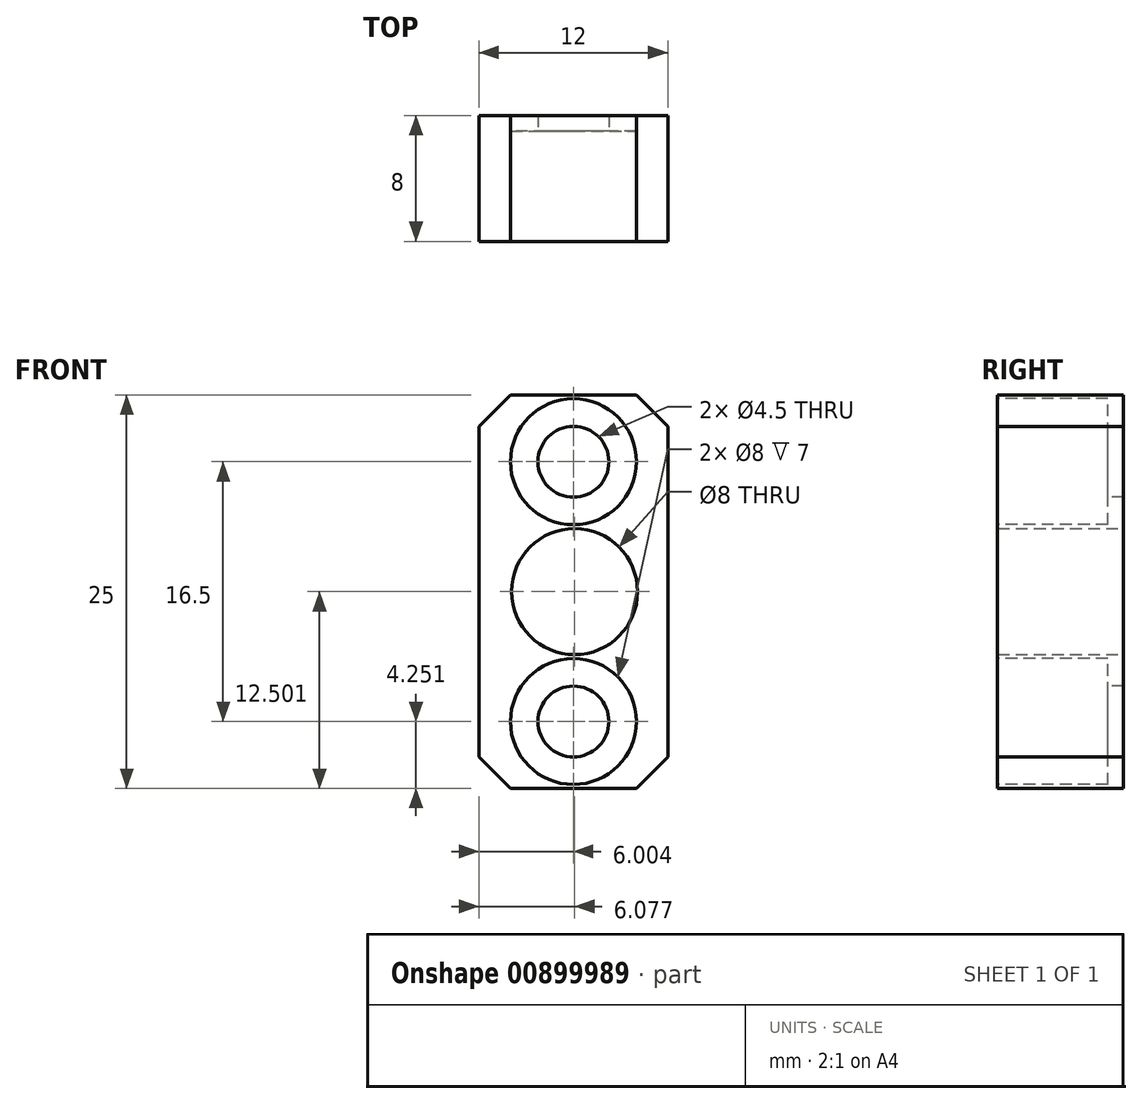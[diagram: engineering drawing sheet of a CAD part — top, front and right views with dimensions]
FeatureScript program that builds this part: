
annotation { "Feature Type Name" : "Feature", "Feature Type Description" : "" }
export const myFeature = defineFeature(function(context is Context, id is Id, definition is map)
    precondition{}
    {
        {
            var Q0;
            Q0=qCreatedBy(makeId("Front.planeOp"),FACE);
            var sketch = newSketch(context, id + "F0", { "sketchPlane" : qUnion([Q0])});
            skLineSegment(sketch, "E0.bottom", {"start": v(-4.19, 15.77) * mm, "end": v(7.81, 15.77) * mm});
            skLineSegment(sketch, "E0.top", {"start": v(-4.19, -9.23) * mm, "end": v(7.81, -9.23) * mm});
            skLineSegment(sketch, "E0.left", {"start": v(-4.19, 15.77) * mm, "end": v(-4.19, -9.23) * mm});
            skLineSegment(sketch, "E0.right", {"start": v(7.81, 15.77) * mm, "end": v(7.81, -9.23) * mm});
            skPoint(sketch, "E1.centerSnap0", {"position": v(1.81, -9.23) * mm});
            skSolve(sketch);
        }
        {
            var Q0;
            Q0=makeQuery(id+"F0.imprint","IMPRINT",FACE,{"disambiguationData":[TD([[makeQuery(id+"F0.imprint","IMPRINT",EDGE,{"derivedFrom":sQuery(id+"F0.wireOp",EDGE,"E0.bottom")}),-1.0]])]});
            extrude(context, id + "F1", {"entities" : qUnion([Q0]), "depth" : 8 * mm, "offsetDistance" : 25 * mm});
        }
        {
            var Q0;
            Q0=makeQuery(id+"F1.opExtrude","SWEPT_EDGE",EDGE,{"disambiguationData":[OSD([sQuery(id+"F0.wireOp",EDGE,"E0.bottom"),sQuery(id+"F0.wireOp",EDGE,"E0.left")])]});
            chamfer(context, id + "F2", {"entities" : qUnion([Q0]), "width" : 2 * mm, "tangentPropagation" : true});
        }
        {
            var Q0;
            Q0=makeQuery(id+"F1.opExtrude","SWEPT_EDGE",EDGE,{"disambiguationData":[OSD([sQuery(id+"F0.wireOp",EDGE,"E0.bottom"),sQuery(id+"F0.wireOp",EDGE,"E0.right")])]});
            var Q1;
            Q1=makeQuery(id+"F1.opExtrude","SWEPT_EDGE",EDGE,{"disambiguationData":[OSD([sQuery(id+"F0.wireOp",EDGE,"E0.top"),sQuery(id+"F0.wireOp",EDGE,"E0.right")])]});
            var Q2;
            Q2=makeQuery(id+"F1.opExtrude","SWEPT_EDGE",EDGE,{"disambiguationData":[OSD([sQuery(id+"F0.wireOp",EDGE,"E0.top"),sQuery(id+"F0.wireOp",EDGE,"E0.left")])]});
            chamfer(context, id + "F3", {"entities" : qUnion([Q0, Q1, Q2]), "width" : 2 * mm, "tangentPropagation" : true});
        }
        {
            var Q0;
            Q0=makeQuery(id+"F1.opExtrude","CAP_FACE",FACE,{"disambiguationData":[OSD([sQuery(id+"F0.wireOp",EDGE,"E0.bottom"),sQuery(id+"F0.wireOp",EDGE,"E0.top"),sQuery(id+"F0.wireOp",EDGE,"E0.left"),sQuery(id+"F0.wireOp",EDGE,"E0.right")])],"isStart":false});
            var sketch = newSketch(context, id + "F4", { "sketchPlane" : qUnion([Q0])});
            skCircle(sketch, "E2", {"center": v(1.81, -4.98) * mm, "radius": 2.25 * mm});
            skPoint(sketch, "E2.centerSnap0", {"position": v(1.81, -9.23) * mm});
            skCircle(sketch, "E3", {"center": v(1.81, 11.52) * mm, "radius": 2.25 * mm});
            skPoint(sketch, "E3.centerSnap0", {"position": v(1.81, 15.77) * mm});
            skSolve(sketch);
        }
        {
            var Q0;
            Q0 = qSketchRegion(id + "F4", true);
            extrude(context, id + "F5", {"entities" : qUnion([Q0]), "operationType" : NewBodyOperationType.REMOVE, "oppositeDirection" : true, "depth" : 25 * mm, "offsetDistance" : 25 * mm});
        }
        {
            var Q0;
            Q0=makeQuery(id+"F1.opExtrude","CAP_FACE",FACE,{"disambiguationData":[OSD([sQuery(id+"F0.wireOp",EDGE,"E0.bottom"),sQuery(id+"F0.wireOp",EDGE,"E0.top"),sQuery(id+"F0.wireOp",EDGE,"E0.left"),sQuery(id+"F0.wireOp",EDGE,"E0.right")])],"isStart":false});
            var sketch = newSketch(context, id + "F6", { "sketchPlane" : qUnion([Q0])});
            skCircle(sketch, "E4", {"center": v(1.81, 11.52) * mm, "radius": 4 * mm});
            skCircle(sketch, "E5", {"center": v(1.81, -4.98) * mm, "radius": 4 * mm});
            skSolve(sketch);
        }
        {
            var Q0;
            Q0 = qSketchRegion(id + "F6", true);
            extrude(context, id + "F7", {"entities" : qUnion([Q0]), "operationType" : NewBodyOperationType.REMOVE, "oppositeDirection" : true, "depth" : 7 * mm, "offsetDistance" : 25 * mm});
        }
        {
            var Q0;
            Q0=qCreatedBy(makeId("Front.planeOp"),FACE);
            var sketch = newSketch(context, id + "F8", { "sketchPlane" : qUnion([Q0])});
            skCircle(sketch, "E6", {"center": v(1.89, 3.27) * mm, "radius": 4 * mm});
            skSolve(sketch);
        }
        {
            var Q0;
            Q0=makeQuery(id+"F8.imprint","IMPRINT",FACE,{"disambiguationData":[TD([[makeQuery(id+"F8.imprint","IMPRINT",EDGE,{"derivedFrom":sQuery(id+"F8.wireOp",EDGE,"E6")}),1.0]])]});
            extrude(context, id + "F9", {"entities" : qUnion([Q0]), "operationType" : NewBodyOperationType.REMOVE, "depth" : 25 * mm, "offsetDistance" : 25 * mm});
        }
    });
